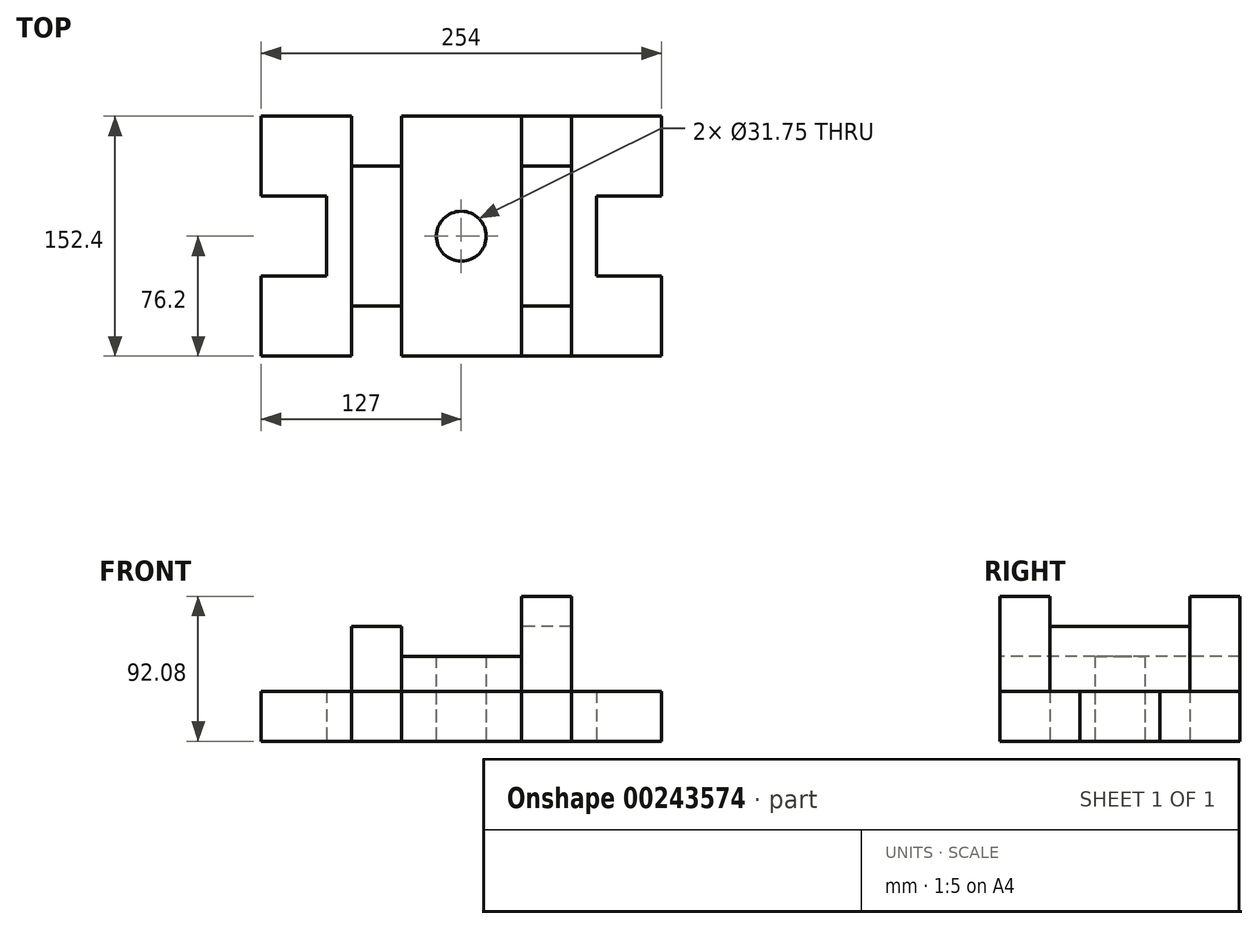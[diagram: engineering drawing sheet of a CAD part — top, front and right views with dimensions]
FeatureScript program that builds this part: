
annotation { "Feature Type Name" : "Feature", "Feature Type Description" : "" }
export const myFeature = defineFeature(function(context is Context, id is Id, definition is map)
    precondition{}
    {
        {
            var Q0;
            Q0=qCreatedBy(makeId("Top.planeOp"),FACE);
            var sketch = newSketch(context, id + "F0", { "sketchPlane" : qUnion([Q0])});
            skLineSegment(sketch, "E0.bottom", {"start": v(-127, 76.2) * mm, "end": v(127, 76.2) * mm});
            skLineSegment(sketch, "E0.top", {"start": v(-127, -76.2) * mm, "end": v(127, -76.2) * mm});
            skLineSegment(sketch, "E0.left", {"start": v(-127, 76.2) * mm, "end": v(-127, 25.4) * mm});
            skLineSegment(sketch, "E0.right", {"start": v(127, 76.2) * mm, "end": v(127, 25.4) * mm});
            skLineSegment(sketch, "E1.bottom", {"start": v(-127, 25.4) * mm, "end": v(-85.72, 25.4) * mm});
            skLineSegment(sketch, "E1.top", {"start": v(-127, -25.4) * mm, "end": v(-85.72, -25.4) * mm});
            skLineSegment(sketch, "E1.right", {"start": v(-85.72, 25.4) * mm, "end": v(-85.72, -25.4) * mm});
            skLineSegment(sketch, "E2.trimOffspring", {"start": v(-127, -25.4) * mm, "end": v(-127, -76.2) * mm});
            skLineSegment(sketch, "E3.MirrorCS", {"start": v(127, 25.4) * mm, "end": v(85.72, 25.4) * mm});
            skLineSegment(sketch, "E4.MirrorCS", {"start": v(85.72, 25.4) * mm, "end": v(85.72, -25.4) * mm});
            skLineSegment(sketch, "E5.MirrorCS", {"start": v(127, -25.4) * mm, "end": v(85.72, -25.4) * mm});
            skLineSegment(sketch, "E6.trimOffspring", {"start": v(127, -25.4) * mm, "end": v(127, -76.2) * mm});
            skLineSegment(sketch, "E7.bottom", {"start": v(-69.85, 76.2) * mm, "end": v(-38.1, 76.2) * mm});
            skLineSegment(sketch, "E7.top", {"start": v(-69.85, -76.2) * mm, "end": v(-38.1, -76.2) * mm});
            skLineSegment(sketch, "E7.left", {"start": v(-69.85, 76.2) * mm, "end": v(-69.85, -76.2) * mm});
            skLineSegment(sketch, "E7.right", {"start": v(-38.1, 76.2) * mm, "end": v(-38.1, -76.2) * mm});
            skLineSegment(sketch, "E8.bottom", {"start": v(27.24, 76.2) * mm, "end": v(69.14, 76.2) * mm});
            skLineSegment(sketch, "E8.top", {"start": v(27.24, -76.2) * mm, "end": v(69.14, -76.2) * mm});
            skCircle(sketch, "E9", {"center": v(0, 0) * mm, "radius": 15.88 * mm});
            skLineSegment(sketch, "E10", {"start": v(-69.85, -44.45) * mm, "end": v(-38.1, -44.45) * mm});
            skLineSegment(sketch, "E11", {"start": v(-69.85, 44.45) * mm, "end": v(-38.1, 44.45) * mm});
            skLineSegment(sketch, "E12.MirrorCS", {"start": v(38.1, 76.2) * mm, "end": v(38.1, -76.2) * mm});
            skLineSegment(sketch, "E13.MirrorCS", {"start": v(69.85, 76.2) * mm, "end": v(69.85, -76.2) * mm});
            skLineSegment(sketch, "E14.MirrorCS", {"start": v(69.85, 44.45) * mm, "end": v(38.1, 44.45) * mm});
            skLineSegment(sketch, "E15.MirrorCS", {"start": v(69.85, -44.45) * mm, "end": v(38.1, -44.45) * mm});
            skSolve(sketch);
        }
        {
            var Q0;
            {var subQ0=sQuery(id+"F0.wireOp",EDGE,"E0.left");Q0=makeQuery(id+"F0.imprint","IMPRINT",FACE,{"disambiguationData":[TD([[makeQuery(id+"F0.imprint","IMPRINT",EDGE,{"derivedFrom":subQ0}),1.0]])]});}
            var Q1;
            {var subQ0=sQuery(id+"F0.wireOp",EDGE,"E7.top");Q1=makeQuery(id+"F0.imprint","IMPRINT",FACE,{"disambiguationData":[TD([[makeQuery(id+"F0.imprint","IMPRINT",EDGE,{"derivedFrom":subQ0}),1.0]])]});}
            var Q2;
            {var subQ0=sQuery(id+"F0.wireOp",EDGE,"E14.MirrorCS");Q2=makeQuery(id+"F0.imprint","IMPRINT",FACE,{"disambiguationData":[TD([[makeQuery(id+"F0.imprint","IMPRINT",EDGE,{"derivedFrom":subQ0}),1.0]])]});}
            var Q3;
            {var subQ4=sQuery(id+"F0.wireOp",EDGE,"E0.right");Q3=makeQuery(id+"F0.imprint","IMPRINT",FACE,{"disambiguationData":[TD([[makeQuery(id+"F0.imprint","IMPRINT",EDGE,{"derivedFrom":subQ4}),-1.0]])]});}
            var Q4;
            {var subQ3=sQuery(id+"F0.wireOp",EDGE,"E15.MirrorCS");Q4=makeQuery(id+"F0.imprint","IMPRINT",FACE,{"disambiguationData":[TD([[makeQuery(id+"F0.imprint","IMPRINT",EDGE,{"derivedFrom":subQ3}),1.0]])]});}
            var Q5;
            {var subQ3=sQuery(id+"F0.wireOp",EDGE,"E14.MirrorCS");Q5=makeQuery(id+"F0.imprint","IMPRINT",FACE,{"disambiguationData":[TD([[makeQuery(id+"F0.imprint","IMPRINT",EDGE,{"derivedFrom":subQ3}),-1.0]])]});}
            var Q6;
            Q6=makeQuery(id+"F0.imprint","IMPRINT",FACE,{"disambiguationData":[TD([[makeQuery(id+"F0.imprint","IMPRINT",EDGE,{"derivedFrom":sQuery(id+"F0.wireOp",EDGE,"E9")}),-1.0]])]});
            var Q7;
            {var subQ0=sQuery(id+"F0.wireOp",EDGE,"E7.bottom");Q7=makeQuery(id+"F0.imprint","IMPRINT",FACE,{"disambiguationData":[TD([[makeQuery(id+"F0.imprint","IMPRINT",EDGE,{"derivedFrom":subQ0}),-1.0]])]});}
            var Q8;
            {var subQ0=sQuery(id+"F0.wireOp",EDGE,"E10");Q8=makeQuery(id+"F0.imprint","IMPRINT",FACE,{"disambiguationData":[TD([[makeQuery(id+"F0.imprint","IMPRINT",EDGE,{"derivedFrom":subQ0}),1.0]])]});}
            var Q9;
            Q9=sQuery(id+"F0.wireOp",EDGE,"E0.top");
            var Q10;
            Q10=sQuery(id+"F0.wireOp",EDGE,"E0.left");
            var Q11;
            Q11=sQuery(id+"F0.wireOp",EDGE,"E0.right");
            var Q12;
            Q12=sQuery(id+"F0.wireOp",EDGE,"E1.bottom");
            var Q13;
            Q13=sQuery(id+"F0.wireOp",EDGE,"E2.trimOffspring");
            var Q14;
            Q14=sQuery(id+"F0.wireOp",EDGE,"E1.top");
            var Q15;
            Q15=sQuery(id+"F0.wireOp",EDGE,"E1.right");
            var Q16;
            Q16=sQuery(id+"F0.wireOp",EDGE,"E7.right");
            var Q17;
            Q17=sQuery(id+"F0.wireOp",EDGE,"E3.MirrorCS");
            var Q18;
            Q18=sQuery(id+"F0.wireOp",EDGE,"E0.bottom");
            var Q19;
            Q19=sQuery(id+"F0.wireOp",EDGE,"E7.left");
            var Q20;
            Q20=sQuery(id+"F0.wireOp",EDGE,"E15.MirrorCS");
            var Q21;
            Q21=sQuery(id+"F0.wireOp",EDGE,"E10");
            var Q22;
            Q22=sQuery(id+"F0.wireOp",EDGE,"E12.MirrorCS");
            var Q23;
            Q23=sQuery(id+"F0.wireOp",EDGE,"E4.MirrorCS");
            var Q24;
            Q24=sQuery(id+"F0.wireOp",EDGE,"E5.MirrorCS");
            var Q25;
            Q25=sQuery(id+"F0.wireOp",EDGE,"E6.trimOffspring");
            var Q26;
            Q26=sQuery(id+"F0.wireOp",EDGE,"E13.MirrorCS");
            var Q27;
            Q27=sQuery(id+"F0.wireOp",EDGE,"E14.MirrorCS");
            var Q28;
            Q28=sQuery(id+"F0.wireOp",EDGE,"E11");
            var Q29;
            Q29=sQuery(id+"F0.wireOp",EDGE,"E7.bottom");
            var Q30;
            Q30=sQuery(id+"F0.wireOp",EDGE,"E9");
            var Q31;
            Q31=sQuery(id+"F0.wireOp",EDGE,"E8.bottom");
            var Q32;
            Q32=sQuery(id+"F0.wireOp",EDGE,"E7.top");
            var Q33;
            Q33=sQuery(id+"F0.wireOp",EDGE,"E8.top");
            extrude(context, id + "F1", {"entities" : qUnion([Q0, Q1, Q2, Q3, Q4, Q5, Q6, Q7, Q8]), "surfaceEntities" : qUnion([Q9, Q10, Q11, Q12, Q13, Q14, Q15, Q16, Q17, Q18, Q19, Q20, Q21, Q22, Q23, Q24, Q25, Q26, Q27, Q28, Q29, Q30, Q31, Q32, Q33]), "depth" : 31.75 * mm});
        }
        {
            var Q0;
            {var subQ0=sQuery(id+"F0.wireOp",EDGE,"E7.bottom");Q0=makeQuery(id+"F0.imprint","IMPRINT",FACE,{"disambiguationData":[TD([[makeQuery(id+"F0.imprint","IMPRINT",EDGE,{"derivedFrom":subQ0}),-1.0]])]});}
            var Q1;
            {var subQ0=sQuery(id+"F0.wireOp",EDGE,"E7.top");Q1=makeQuery(id+"F0.imprint","IMPRINT",FACE,{"disambiguationData":[TD([[makeQuery(id+"F0.imprint","IMPRINT",EDGE,{"derivedFrom":subQ0}),1.0]])]});}
            var Q2;
            {var subQ3=sQuery(id+"F0.wireOp",EDGE,"E14.MirrorCS");Q2=makeQuery(id+"F0.imprint","IMPRINT",FACE,{"disambiguationData":[TD([[makeQuery(id+"F0.imprint","IMPRINT",EDGE,{"derivedFrom":subQ3}),-1.0]])]});}
            var Q3;
            {var subQ3=sQuery(id+"F0.wireOp",EDGE,"E15.MirrorCS");Q3=makeQuery(id+"F0.imprint","IMPRINT",FACE,{"disambiguationData":[TD([[makeQuery(id+"F0.imprint","IMPRINT",EDGE,{"derivedFrom":subQ3}),1.0]])]});}
            extrude(context, id + "F2", {"entities" : qUnion([Q0, Q1, Q2, Q3]), "depth" : 92.07 * mm});
        }
        {
            var Q0;
            {var subQ0=sQuery(id+"F0.wireOp",EDGE,"E10");Q0=makeQuery(id+"F0.imprint","IMPRINT",FACE,{"disambiguationData":[TD([[makeQuery(id+"F0.imprint","IMPRINT",EDGE,{"derivedFrom":subQ0}),1.0]])]});}
            var Q1;
            {var subQ0=sQuery(id+"F0.wireOp",EDGE,"E14.MirrorCS");Q1=makeQuery(id+"F0.imprint","IMPRINT",FACE,{"disambiguationData":[TD([[makeQuery(id+"F0.imprint","IMPRINT",EDGE,{"derivedFrom":subQ0}),1.0]])]});}
            extrude(context, id + "F3", {"entities" : qUnion([Q0, Q1]), "depth" : 73.02 * mm});
        }
        {
            var Q0;
            Q0=makeQuery(id+"F0.imprint","IMPRINT",FACE,{"disambiguationData":[TD([[makeQuery(id+"F0.imprint","IMPRINT",EDGE,{"derivedFrom":sQuery(id+"F0.wireOp",EDGE,"E9")}),-1.0]])]});
            extrude(context, id + "F4", {"entities" : qUnion([Q0]), "depth" : 53.97 * mm});
        }
    });
